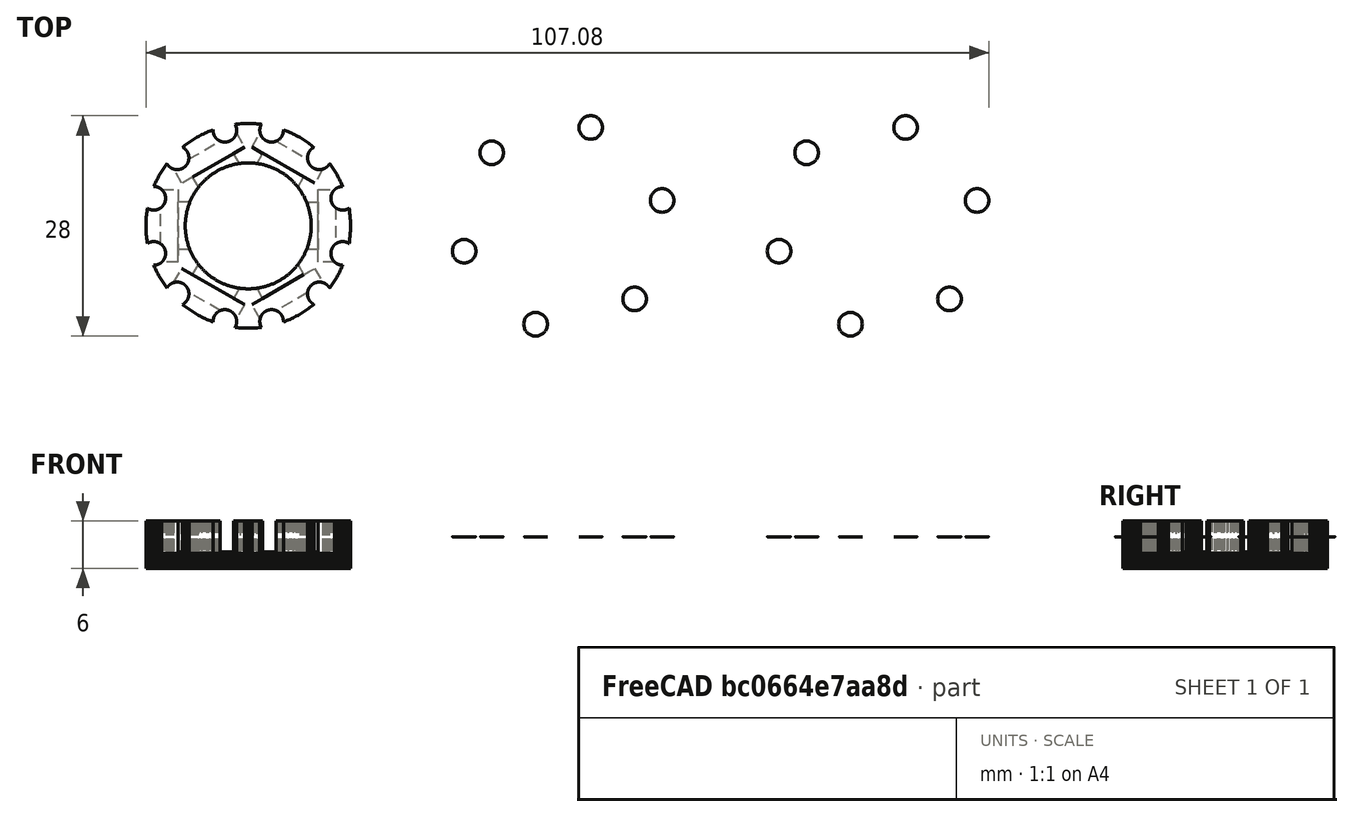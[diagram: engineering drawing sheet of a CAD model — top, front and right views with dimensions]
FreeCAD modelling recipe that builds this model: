
FCSTD DOCUMENT  (FreeCAD 0.16R)
Label: cut_lens75_h8mm
License: All rights reserved
LicenseURL: http://en.wikipedia.org/wiki/All_rights_reserved
objects: Part::Part2DObjectPython×9, Part::FeaturePython×4, App::DocumentObjectGroup×3, Sketcher::SketchObject×1, Part::Feature×1
note: 15 computed .brp shape members not serialized (recipe doc carries the construction recipe); baked Part::Feature solids carry a one-line shape summary decoded from their .brp

FEATURE [Part::Part2DObjectPython] Circle004  # Draft 2D object (typed FeaturePython)
  FirstAngle = 0
  LastAngle = 0
  MakeFace = true
  Placement = pos=(3.5,-12.5,0) rot=(1,0,0;3.14159rad)
  Radius = 1.5
FEATURE [Part::Part2DObjectPython] Circle005  # Draft 2D object (typed FeaturePython)
  FirstAngle = 0
  LastAngle = 0
  MakeFace = true
  Placement = pos=(-3.5,-12.5,0) rot=(1,0,0;3.14159rad)
  Radius = 1.5
FEATURE [Part::FeaturePython] Array  # Draft array (typed FeaturePython)
  Angle = 360
  ArrayType = 1
  Axis = (0,0,1)
  Base = -> Circle005
  Center = (0,0,0)
  Fuse = false
  IntervalAxis = (0,0,0)
  IntervalX = (0,0,0)
  IntervalY = (0,0,0)
  IntervalZ = (0,0,0)
  NumberPolar = 6
  NumberX = 1
  NumberY = 1
  NumberZ = 1
FEATURE [Part::FeaturePython] Array001  # Draft array (typed FeaturePython)
  Angle = 360
  ArrayType = 1
  Axis = (0,0,1)
  Base = -> Circle004
  Center = (0,0,0)
  Fuse = false
  IntervalAxis = (0,0,0)
  IntervalX = (1,0,0)
  IntervalY = (0,1,0)
  IntervalZ = (0,0,0)
  NumberPolar = 6
  NumberX = 2
  NumberY = 2
  NumberZ = 1
FEATURE [Part::Part2DObjectPython] Circle  # Draft 2D object (typed FeaturePython)
  FirstAngle = 0
  LastAngle = 0
  MakeFace = true
  Placement = pos=(0,0,0) rot=(1,0,0;3.14159rad)
  Radius = 13
FEATURE [Part::Part2DObjectPython] Circle006  # Draft 2D object (typed FeaturePython)
  FirstAngle = 0
  LastAngle = 0
  MakeFace = true
  Placement = pos=(0,0,0) rot=(1,0,0;3.14159rad)
  Radius = 4.05
FEATURE [Part::Part2DObjectPython] Circle007  # Draft 2D object (typed FeaturePython)
  FirstAngle = 0
  LastAngle = 0
  MakeFace = true
  Placement = pos=(0,0,0) rot=(1,0,0;3.14159rad)
  Radius = 4.61
FEATURE [App::DocumentObjectGroup] Groupe  label="lens_stand"
  Group = -> [Array,Array001,Circle,Circle006,Circle007]
FEATURE [Part::Part2DObjectPython] Circle008  # Draft 2D object (typed FeaturePython)
  FirstAngle = 0
  LastAngle = 0
  MakeFace = false
  Placement = pos=(40,0,0) rot=(1,0,0;3.14159rad)
  Radius = 13
FEATURE [Part::Part2DObjectPython] Circle009  # Draft 2D object (typed FeaturePython)
  FirstAngle = 0
  LastAngle = 0
  MakeFace = true
  Placement = pos=(43.5,-12.5,0) rot=(0,0,1;0rad)
  Radius = 1.5
FEATURE [Part::Part2DObjectPython] Circle010  # Draft 2D object (typed FeaturePython)
  FirstAngle = 0
  LastAngle = 0
  MakeFace = true
  Placement = pos=(36.5,-12.5,0) rot=(0,0,1;0rad)
  Radius = 1.5
FEATURE [Part::FeaturePython] Array002  # Draft array (typed FeaturePython)
  Angle = 360
  ArrayType = 1
  Axis = (0,0,1)
  Base = -> Circle010
  Center = (40,0,0)
  Fuse = false
  IntervalAxis = (0,0,0)
  IntervalX = (0,0,0)
  IntervalY = (0,0,0)
  IntervalZ = (0,0,0)
  NumberPolar = 6
  NumberX = 1
  NumberY = 1
  NumberZ = 1
FEATURE [Part::FeaturePython] Array003  # Draft array (typed FeaturePython)
  Angle = 360
  ArrayType = 1
  Axis = (0,0,1)
  Base = -> Circle009
  Center = (40,0,0)
  Fuse = false
  IntervalAxis = (0,0,0)
  IntervalX = (0,0,0)
  IntervalY = (0,0,0)
  IntervalZ = (0,0,0)
  NumberPolar = 6
  NumberX = 1
  NumberY = 1
  NumberZ = 1
FEATURE [Part::Part2DObjectPython] Circle011  # Draft 2D object (typed FeaturePython)
  FirstAngle = 0
  LastAngle = 0
  MakeFace = true
  Placement = pos=(40,0,0) rot=(1,0,0;3.14159rad)
  Radius = 4
FEATURE [Sketcher::SketchObject] Sketch
  sketch-geometry (5):
    g0: LineSegment StartX=35.75 StartY=4.25 StartZ=0 EndX=50.0853 EndY=4.25 EndZ=0
    g1: LineSegment StartX=50.0853 StartY=-4.25 StartZ=0 EndX=35.75 EndY=-4.25 EndZ=0
    g2: LineSegment StartX=35.75 StartY=-4.25 StartZ=0 EndX=35.75 EndY=4.25 EndZ=0
    g3: Circle CenterX=39.9395 CenterY=0 CenterZ=0 NormalX=0 NormalY=0 NormalZ=-1 Radius=16
    g4: ArcOfCircle CenterX=39.9395 CenterY=0 CenterZ=0 NormalX=0 NormalY=0 NormalZ=1 Radius=11 StartAngle=0.396686 EndAngle=5.8865
  constraints (13):
    c: Horizontal(g0)
    c: Horizontal(g1)
    c: Vertical(g2)
    c: Radius(g4) = 11
    c: Coincident(g0,g2)
    c: PointOnObject(g0,g4)
    c: Coincident(g0,g4)
    c: PointOnObject(g1,g4)
    c: Coincident(g1,g2)
    c: Coincident(g1,g4)
    c: DistanceY(g2,g2) = 8.5
    c: Symmetric(g0,g1,g-1)
    c: Coincident(g4,g3)
FEATURE [App::DocumentObjectGroup] Groupe001  label="camera_stand"
  Group = -> [Circle008,Circle009,Circle010,Array002,Array003,Circle011,Sketch]
FEATURE [App::DocumentObjectGroup] Groupe002  label="light_stand"
FEATURE [Part::Feature] light_stand001  label="light_stand002"
  shape: bbox 26 x 26 x 6 mm, 12768 faces, 0 solids (baked)
